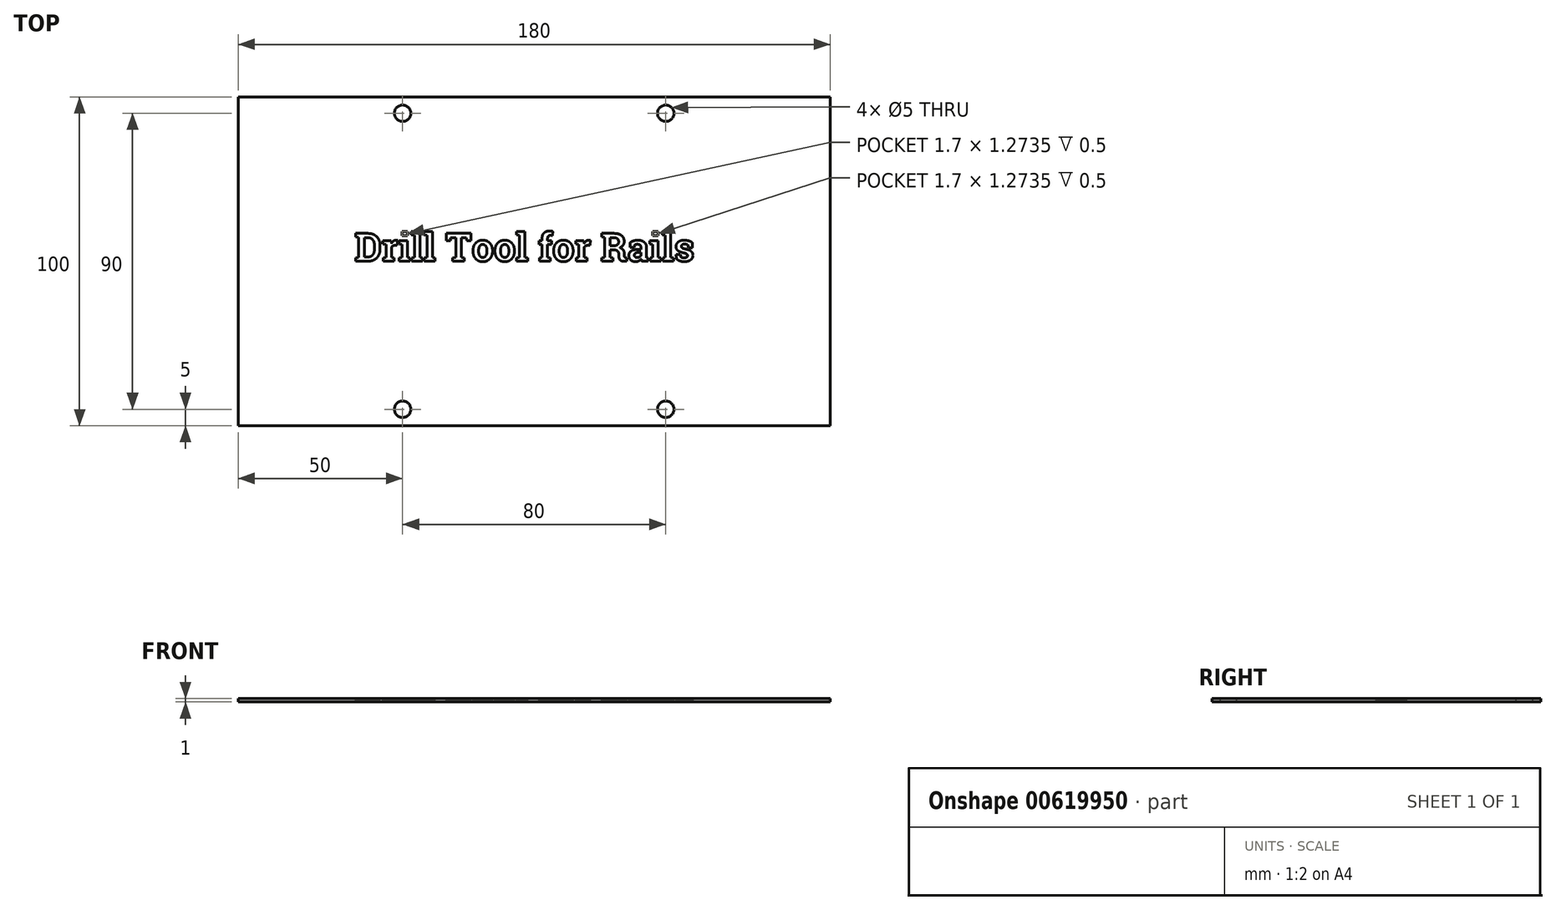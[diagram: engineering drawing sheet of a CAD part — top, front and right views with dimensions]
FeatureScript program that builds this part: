
annotation { "Feature Type Name" : "Feature", "Feature Type Description" : "" }
export const myFeature = defineFeature(function(context is Context, id is Id, definition is map)
    precondition{}
    {
        {
            var Q0;
            Q0=qCreatedBy(makeId("Top.planeOp"),FACE);
            var sketch = newSketch(context, id + "F0", { "sketchPlane" : qUnion([Q0])});
            skLineSegment(sketch, "E0.bottom", {"start": v(-90, 50) * mm, "end": v(90, 50) * mm});
            skLineSegment(sketch, "E0.top", {"start": v(-90, -50) * mm, "end": v(90, -50) * mm});
            skLineSegment(sketch, "E0.left", {"start": v(-90, 50) * mm, "end": v(-90, -50) * mm});
            skLineSegment(sketch, "E0.right", {"start": v(90, 50) * mm, "end": v(90, -50) * mm});
            skPoint(sketch, "E0.middle", {"position": v(0, 0) * mm});
            skSolve(sketch);
        }
        {
            var Q0;
            Q0=makeQuery(id+"F0.imprint","IMPRINT",FACE,{"disambiguationData":[TD([[makeQuery(id+"F0.imprint","IMPRINT",EDGE,{"derivedFrom":sQuery(id+"F0.wireOp",EDGE,"E0.bottom")}),-1.0]])]});
            extrude(context, id + "F1", {"entities" : qUnion([Q0]), "depth" : 1 * mm, "offsetDistance" : 25 * mm});
        }
        {
            var Q0;
            {var subQ0=sQuery(id+"F0.wireOp",EDGE,"E0.bottom");var subQ1=sQuery(id+"F0.wireOp",EDGE,"E0.right");var subQ2=sQuery(id+"F0.wireOp",EDGE,"E0.left");Q0=makeQuery(id+"FbBjWBlYDKZshwE_1.boolean.opBoolean","SPLIT",FACE,{"disambiguationData":[TD([makeQuery(id+"F1.opExtrude","SWEPT_FACE",FACE,{"disambiguationData":[OSD([subQ0])]})])],"derivedFrom":makeQuery(id+"F1.opExtrude","CAP_FACE",FACE,{"disambiguationData":[OSD([subQ0,sQuery(id+"F0.wireOp",EDGE,"E0.top"),subQ2,subQ1])],"isStart":true})});}
            var sketch = newSketch(context, id + "F2", { "sketchPlane" : qUnion([Q0])});
            skPoint(sketch, "E1", {"position": v(40, 45) * mm});
            skLineSegment(sketch, "E2", {"start": v(0, -50) * mm, "end": v(0, 50.08) * mm, "construction": true});
            skPoint(sketch, "E2.endSnap0", {"position": v(0, -50) * mm});
            skLineSegment(sketch, "E3", {"start": v(0, 0) * mm, "end": v(89.96, 0) * mm, "construction": true});
            skPoint(sketch, "E4.MirrorP", {"position": v(40, -45) * mm});
            skLineSegment(sketch, "E5.MirrorCS", {"start": v(0, 50) * mm, "end": v(0, -50.08) * mm, "construction": true});
            skPoint(sketch, "E6.MirrorP", {"position": v(-40, 45) * mm});
            skPoint(sketch, "E7.MirrorP", {"position": v(-40, -45) * mm});
            skSolve(sketch);
        }
        {
            var Q0;
            Q0=sQuery(id+"F2.wireOp",VERTEX,"E6.MirrorP");
            var Q1;
            Q1=sQuery(id+"F2.wireOp",VERTEX,"E1");
            var Q2;
            Q2=sQuery(id+"F2.wireOp",VERTEX,"E4.MirrorP");
            var Q3;
            Q3=sQuery(id+"F2.wireOp",VERTEX,"E7.MirrorP");
            var Q4;
            Q4=makeQuery(id+"F1.opExtrude","SWEPT_BODY",BODY,{"disambiguationData":[OSD([sQuery(id+"F0.wireOp",EDGE,"E0.bottom"),sQuery(id+"F0.wireOp",EDGE,"E0.top"),sQuery(id+"F0.wireOp",EDGE,"E0.left"),sQuery(id+"F0.wireOp",EDGE,"E0.right")])]});
            hole(context, id + "F3", {"style" : HoleStyle.SIMPLE, "endStyle" : HoleEndStyle.THROUGH, "standardTappedOrClearance" : lookupTablePath({ "standard" : "ISO", "size" : "5", "type" : "Drilled" }), "standardBlindInLast" : lookupTablePath({ "standard" : "ISO", "size" : "5", "type" : "Drilled" }), "holeDiameter" : 5 * mm, "majorDiameter" : 5 * mm, "isTappedThrough" : true, "tappedDepth" : 7.6 * mm, "tapClearance" : 0, "locations" : qUnion([Q0, Q1, Q2, Q3]), "scope" : qUnion([Q4]), "startStyle" : HoleStartStyle.SKETCH});
        }
        {
            var Q0;
            Q0=makeQuery(id+"F1.opExtrude","CAP_FACE",FACE,{"disambiguationData":[OSD([sQuery(id+"F0.wireOp",EDGE,"E0.bottom"),sQuery(id+"F0.wireOp",EDGE,"E0.top"),sQuery(id+"F0.wireOp",EDGE,"E0.left"),sQuery(id+"F0.wireOp",EDGE,"E0.right")])],"isStart":false});
            var sketch = newSketch(context, id + "F4", { "sketchPlane" : qUnion([Q0])});
            skText(sketch, "E8", { "text": "Drill Tool for Rails", "fontName": "RobotoSlab-Bold.ttf"});
            const initialGuessF4  = {"E8": [-0.05457, 0, 1, 0, 0.00858]};
            skSetInitialGuess(sketch, initialGuessF4);
            skSolve(sketch);
        }
        {
            var Q0;
            Q0 = qSketchRegion(id + "F4", true);
            extrude(context, id + "F5", {"entities" : qUnion([Q0]), "operationType" : NewBodyOperationType.REMOVE, "oppositeDirection" : true, "depth" : 0.5 * mm, "offsetDistance" : 25 * mm});
        }
    });
